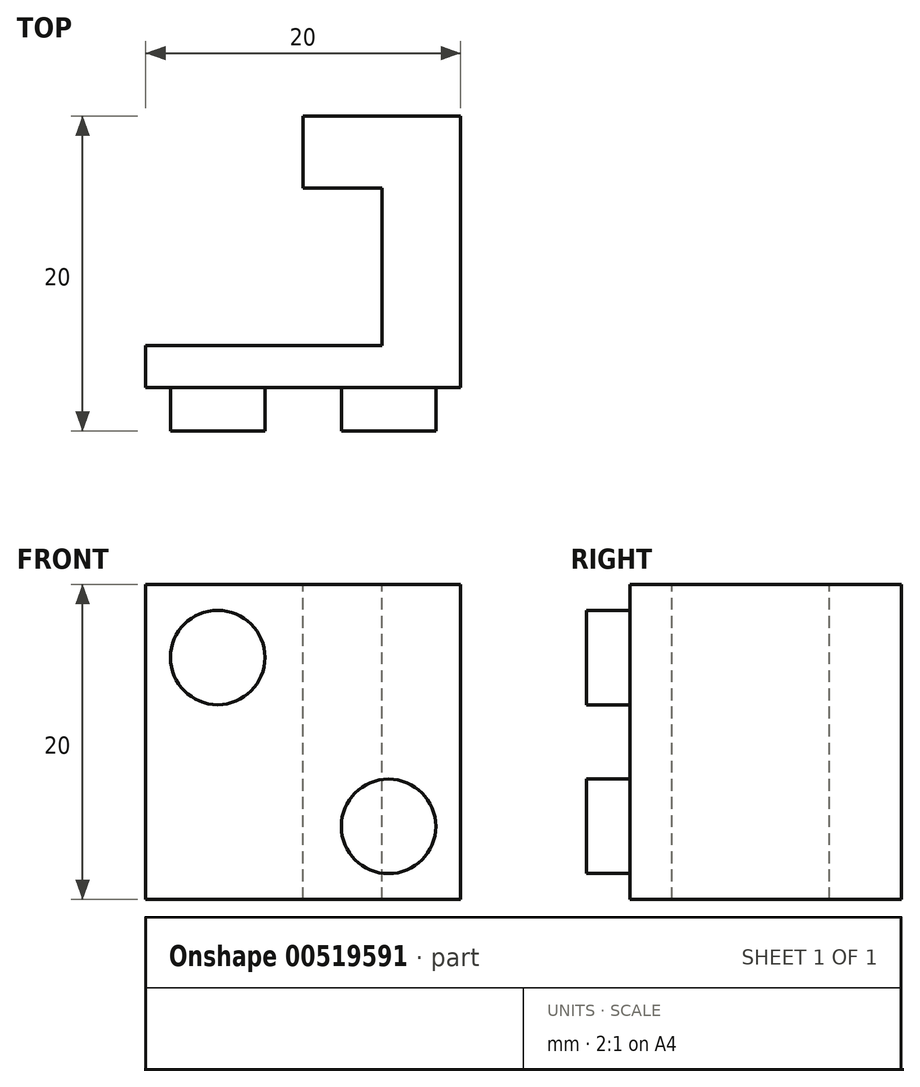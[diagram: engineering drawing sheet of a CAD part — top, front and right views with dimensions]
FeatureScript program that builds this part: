
annotation { "Feature Type Name" : "Feature", "Feature Type Description" : "" }
export const myFeature = defineFeature(function(context is Context, id is Id, definition is map)
    precondition{}
    {
        {
            var Q0;
            Q0=qCreatedBy(makeId("Top.planeOp"),FACE);
            var sketch = newSketch(context, id + "F0", { "sketchPlane" : qUnion([Q0])});
            skLineSegment(sketch, "E0.bottom", {"start": v(10, -10) * mm, "end": v(-10, -10) * mm});
            skLineSegment(sketch, "E0.top", {"start": v(10, 10) * mm, "end": v(-10, 10) * mm});
            skLineSegment(sketch, "E0.left", {"start": v(10, -10) * mm, "end": v(10, 10) * mm});
            skLineSegment(sketch, "E0.right", {"start": v(-10, -10) * mm, "end": v(-10, 10) * mm});
            skPoint(sketch, "E0.middle", {"position": v(0, 0) * mm});
            skSolve(sketch);
        }
        {
            var Q0;
            Q0=makeQuery(id+"F0.imprint","IMPRINT",FACE,{"disambiguationData":[TD([[makeQuery(id+"F0.imprint","IMPRINT",EDGE,{"derivedFrom":sQuery(id+"F0.wireOp",EDGE,"E0.bottom")}),-1.0]])]});
            extrude(context, id + "F1", {"entities" : qUnion([Q0]), "depth" : 20 * mm, "offsetDistance" : 25 * mm});
        }
        {
            var Q0;
            Q0=makeQuery(id+"F1.opExtrude","CAP_FACE",FACE,{"disambiguationData":[OSD([sQuery(id+"F0.wireOp",EDGE,"E0.bottom"),sQuery(id+"F0.wireOp",EDGE,"E0.top"),sQuery(id+"F0.wireOp",EDGE,"E0.left"),sQuery(id+"F0.wireOp",EDGE,"E0.right")])],"isStart":false});
            var sketch = newSketch(context, id + "F2", { "sketchPlane" : qUnion([Q0])});
            skLineSegment(sketch, "E1.bottom", {"start": v(5, -4.56) * mm, "end": v(-15, -4.56) * mm});
            skLineSegment(sketch, "E1.top", {"start": v(5, 5.44) * mm, "end": v(-15, 5.44) * mm});
            skLineSegment(sketch, "E1.left", {"start": v(5, -4.56) * mm, "end": v(5, 5.44) * mm});
            skLineSegment(sketch, "E1.right", {"start": v(-15, -4.56) * mm, "end": v(-15, 5.44) * mm});
            skLineSegment(sketch, "E2", {"start": v(0, 10) * mm, "end": v(0, 5.44) * mm});
            skSolve(sketch);
        }
        {
            var Q0;
            {var subQ0=sQuery(id+"F2.wireOp",EDGE,"E1.left");Q0=makeQuery(id+"F2.imprint","IMPRINT",FACE,{"disambiguationData":[TD([[makeQuery(id+"F2.imprint","IMPRINT",EDGE,{"derivedFrom":subQ0}),1.0]])]});}
            var Q1;
            {var subQ0=sQuery(id+"F2.wireOp",EDGE,"E2");Q1=makeQuery(id+"F2.imprint","IMPRINT",FACE,{"disambiguationData":[TD([[makeQuery(id+"F2.imprint","IMPRINT",EDGE,{"derivedFrom":subQ0}),-1.0]])]});}
            extrude(context, id + "F3", {"entities" : qUnion([Q0, Q1]), "operationType" : NewBodyOperationType.REMOVE, "oppositeDirection" : true, "depth" : 20 * mm, "offsetDistance" : 25 * mm});
        }
        {
            var Q0;
            Q0=makeQuery(id+"F1.opExtrude","SWEPT_FACE",FACE,{"disambiguationData":[OSD([sQuery(id+"F0.wireOp",EDGE,"E0.bottom")])]});
            var sketch = newSketch(context, id + "F4", { "sketchPlane" : qUnion([Q0])});
            skCircle(sketch, "E3", {"center": v(-5.42, 4.64) * mm, "radius": 3 * mm});
            skLineSegment(sketch, "E4", {"start": v(0, 0) * mm, "end": v(0, 20) * mm, "construction": true});
            skCircle(sketch, "E5.MirrorC", {"center": v(5.42, 4.64) * mm, "radius": 3 * mm});
            skLineSegment(sketch, "E6", {"start": v(-10, 10) * mm, "end": v(10, 10) * mm, "construction": true});
            skCircle(sketch, "E7.MirrorC", {"center": v(5.42, 15.36) * mm, "radius": 3 * mm});
            skCircle(sketch, "E8.MirrorC", {"center": v(-5.42, 15.36) * mm, "radius": 3 * mm});
            skSolve(sketch);
        }
        {
            var Q0;
            Q0=makeQuery(id+"F4.imprint","IMPRINT",FACE,{"disambiguationData":[TD([[makeQuery(id+"F4.imprint","IMPRINT",EDGE,{"derivedFrom":sQuery(id+"F4.wireOp",EDGE,"E3")}),1.0]])]});
            var Q1;
            Q1=makeQuery(id+"F4.imprint","IMPRINT",FACE,{"disambiguationData":[TD([[makeQuery(id+"F4.imprint","IMPRINT",EDGE,{"derivedFrom":sQuery(id+"F4.wireOp",EDGE,"E8.MirrorC")}),-1.0]])]});
            var Q2;
            Q2=makeQuery(id+"F4.imprint","IMPRINT",FACE,{"disambiguationData":[TD([[makeQuery(id+"F4.imprint","IMPRINT",EDGE,{"derivedFrom":sQuery(id+"F4.wireOp",EDGE,"E7.MirrorC")}),1.0]])]});
            var Q3;
            Q3=makeQuery(id+"F4.imprint","IMPRINT",FACE,{"disambiguationData":[TD([[makeQuery(id+"F4.imprint","IMPRINT",EDGE,{"derivedFrom":sQuery(id+"F4.wireOp",EDGE,"E5.MirrorC")}),-1.0]])]});
            extrude(context, id + "F5", {"entities" : qUnion([Q0, Q1, Q2, Q3]), "operationType" : NewBodyOperationType.REMOVE, "oppositeDirection" : true, "depth" : 2.75 * mm, "offsetDistance" : 25 * mm});
        }
    });
